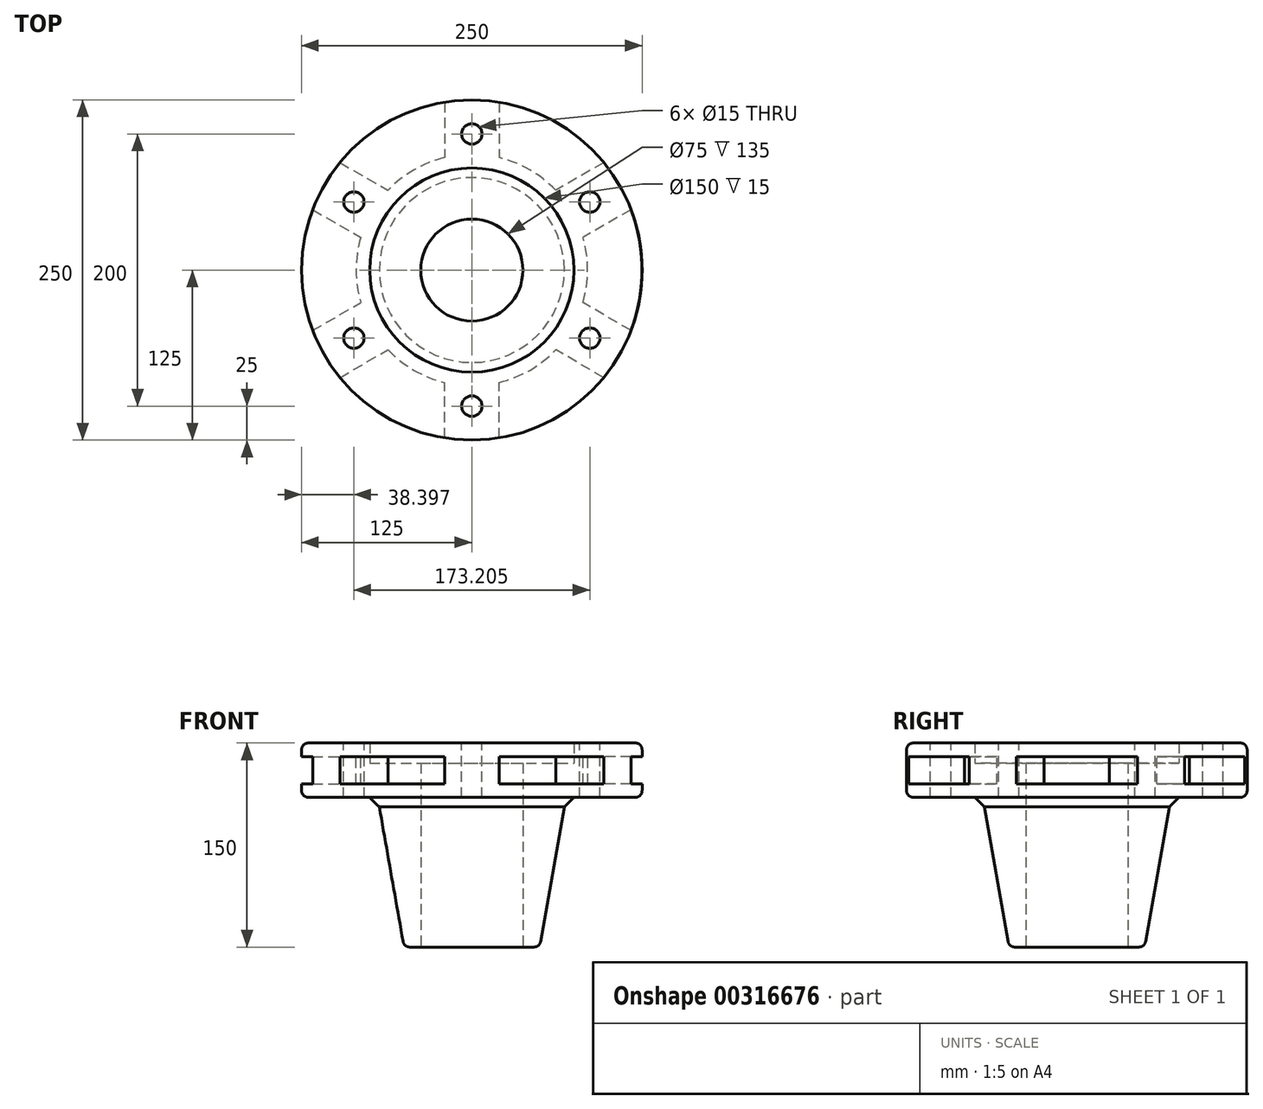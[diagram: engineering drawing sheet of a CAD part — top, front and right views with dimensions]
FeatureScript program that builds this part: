
annotation { "Feature Type Name" : "Feature", "Feature Type Description" : "" }
export const myFeature = defineFeature(function(context is Context, id is Id, definition is map)
    precondition{}
    {
        {
            var Q0;
            Q0=qCreatedBy(makeId("Front.planeOp"),FACE);
            var sketch = newSketch(context, id + "F0", { "sketchPlane" : qUnion([Q0])});
            skLineSegment(sketch, "E0", {"start": v(0, 0) * mm, "end": v(0, 150) * mm, "construction": true});
            skLineSegment(sketch, "E1", {"start": v(-37.5, 135) * mm, "end": v(-37.5, 0) * mm});
            skLineSegment(sketch, "E2", {"start": v(-37.5, 0) * mm, "end": v(-49.78, 0) * mm});
            skLineSegment(sketch, "E3", {"start": v(-49.78, 0) * mm, "end": v(-67.93, 102.93) * mm});
            skLineSegment(sketch, "E4", {"start": v(-75, 110) * mm, "end": v(-125, 110) * mm});
            skLineSegment(sketch, "E5", {"start": v(-125, 110) * mm, "end": v(-125, 150) * mm});
            skLineSegment(sketch, "E6", {"start": v(-125, 150) * mm, "end": v(-75, 150) * mm});
            skLineSegment(sketch, "E7", {"start": v(-75, 150) * mm, "end": v(-75, 135) * mm});
            skLineSegment(sketch, "E8", {"start": v(-75, 135) * mm, "end": v(-37.5, 135) * mm});
            skLineSegment(sketch, "E9", {"start": v(-67.93, 102.93) * mm, "end": v(-75, 110) * mm});
            skSolve(sketch);
        }
        {
            var Q0;
            Q0=makeQuery(id+"F0.imprint","IMPRINT",FACE,{"disambiguationData":[TD([[makeQuery(id+"F0.imprint","IMPRINT",EDGE,{"derivedFrom":sQuery(id+"F0.wireOp",EDGE,"E1")}),-1.0]])]});
            var Q1;
            Q1=sQuery(id+"F0.wireOp",EDGE,"E0");
            revolve(context, id + "F1", {"entities" : qUnion([Q0]), "axis" : qUnion([Q1]), "revolveType" : RevolveType.FULL});
        }
        {
            var Q0;
            Q0=makeQuery(id+"F1.opRevolve","SWEPT_FACE",FACE,{"disambiguationData":[OSD([sQuery(id+"F0.wireOp",EDGE,"E6")])]});
            cPlane(context, id + "F2", {"entities" : qUnion([Q0]), "cplaneType" : CPlaneType.OFFSET, "offset" : 10 * mm, "oppositeDirection" : true, "width" : 150 * mm, "height" : 150 * mm});
        }
        {
            var Q0;
            Q0=qCreatedBy(id+"F2.planeOp",FACE);
            var sketch = newSketch(context, id + "F3", { "sketchPlane" : qUnion([Q0])});
            skCircle(sketch, "E10", {"center": v(0, 0) * mm, "radius": 85 * mm});
            skCircle(sketch, "E11", {"center": v(0, 0) * mm, "radius": 100 * mm, "construction": true});
            skPoint(sketch, "E12", {"position": v(0, 100) * mm});
            skPoint(sketch, "E13.1.0", {"position": v(-86.6, 50) * mm});
            skPoint(sketch, "E13.2.0", {"position": v(-86.6, -50) * mm});
            skPoint(sketch, "E13.3.0", {"position": v(0, -100) * mm});
            skPoint(sketch, "E13.4.0", {"position": v(86.6, -50) * mm});
            skPoint(sketch, "E13.5.0", {"position": v(86.6, 50) * mm});
            skLineSegment(sketch, "E14", {"start": v(-20, 123.39) * mm, "end": v(-20, 82.61) * mm});
            skLineSegment(sketch, "E15", {"start": v(20, 123.39) * mm, "end": v(20, 82.61) * mm});
            skPoint(sketch, "E16.center", {"position": v(-16.81, 5.93) * mm});
            skCircle(sketch, "E17", {"center": v(0, 0) * mm, "radius": 125 * mm});
            skLineSegment(sketch, "E18.1.0", {"start": v(-116.86, 44.37) * mm, "end": v(-81.55, 23.99) * mm});
            skLineSegment(sketch, "E18.1.1", {"start": v(-96.86, 79.02) * mm, "end": v(-61.55, 58.63) * mm});
            skLineSegment(sketch, "E18.2.0", {"start": v(-96.86, -79.02) * mm, "end": v(-61.55, -58.63) * mm});
            skLineSegment(sketch, "E18.2.1", {"start": v(-116.86, -44.37) * mm, "end": v(-81.55, -23.99) * mm});
            skLineSegment(sketch, "E18.3.0", {"start": v(20, -123.39) * mm, "end": v(20, -82.61) * mm});
            skLineSegment(sketch, "E18.3.1", {"start": v(-20, -123.39) * mm, "end": v(-20, -82.61) * mm});
            skLineSegment(sketch, "E18.4.0", {"start": v(116.86, -44.37) * mm, "end": v(81.55, -23.99) * mm});
            skLineSegment(sketch, "E18.4.1", {"start": v(96.86, -79.02) * mm, "end": v(61.55, -58.63) * mm});
            skLineSegment(sketch, "E18.5.0", {"start": v(96.86, 79.02) * mm, "end": v(61.55, 58.63) * mm});
            skLineSegment(sketch, "E18.5.1", {"start": v(116.86, 44.37) * mm, "end": v(81.55, 23.99) * mm});
            skSolve(sketch);
        }
        {
            var Q0;
            {var subQ0=sQuery(id+"F3.wireOp",EDGE,"E14");Q0=makeQuery(id+"F3.imprint","IMPRINT",FACE,{"disambiguationData":[TD([[makeQuery(id+"F3.imprint","IMPRINT",EDGE,{"derivedFrom":subQ0}),-1.0]])]});}
            var Q1;
            {var subQ0=sQuery(id+"F3.wireOp",EDGE,"E15");Q1=makeQuery(id+"F3.imprint","IMPRINT",FACE,{"disambiguationData":[TD([[makeQuery(id+"F3.imprint","IMPRINT",EDGE,{"derivedFrom":subQ0}),1.0]])]});}
            var Q2;
            {var subQ0=sQuery(id+"F3.wireOp",EDGE,"E18.4.0");Q2=makeQuery(id+"F3.imprint","IMPRINT",FACE,{"disambiguationData":[TD([[makeQuery(id+"F3.imprint","IMPRINT",EDGE,{"derivedFrom":subQ0}),-1.0]])]});}
            var Q3;
            {var subQ0=sQuery(id+"F3.wireOp",EDGE,"E18.3.0");Q3=makeQuery(id+"F3.imprint","IMPRINT",FACE,{"disambiguationData":[TD([[makeQuery(id+"F3.imprint","IMPRINT",EDGE,{"derivedFrom":subQ0}),-1.0]])]});}
            var Q4;
            {var subQ0=sQuery(id+"F3.wireOp",EDGE,"E18.2.0");Q4=makeQuery(id+"F3.imprint","IMPRINT",FACE,{"disambiguationData":[TD([[makeQuery(id+"F3.imprint","IMPRINT",EDGE,{"derivedFrom":subQ0}),-1.0]])]});}
            var Q5;
            {var subQ0=sQuery(id+"F3.wireOp",EDGE,"E18.1.0");Q5=makeQuery(id+"F3.imprint","IMPRINT",FACE,{"disambiguationData":[TD([[makeQuery(id+"F3.imprint","IMPRINT",EDGE,{"derivedFrom":subQ0}),-1.0]])]});}
            extrude(context, id + "F4", {"entities" : qUnion([Q0, Q1, Q2, Q3, Q4, Q5]), "operationType" : NewBodyOperationType.REMOVE, "oppositeDirection" : true, "depth" : 20 * mm});
        }
        {
            var Q0;
            Q0=makeQuery(id+"F1.opRevolve","SWEPT_EDGE",EDGE,{"disambiguationData":[OSD([sQuery(id+"F0.wireOp",EDGE,"E5"),sQuery(id+"F0.wireOp",EDGE,"E6")])]});
            var Q1;
            Q1=makeQuery(id+"F1.opRevolve","SWEPT_EDGE",EDGE,{"disambiguationData":[OSD([sQuery(id+"F0.wireOp",EDGE,"E4"),sQuery(id+"F0.wireOp",EDGE,"E5")])]});
            var Q2;
            Q2=makeQuery(id+"F1.opRevolve","SWEPT_EDGE",EDGE,{"disambiguationData":[OSD([sQuery(id+"F0.wireOp",EDGE,"E2"),sQuery(id+"F0.wireOp",EDGE,"E3")])]});
            fillet(context, id + "F5", {"entities" : qUnion([Q0, Q1, Q2]), "radius" : 5 * mm, "tangentPropagation" : true, "allowEdgeOverflow" : false});
        }
        {
            var Q0;
            Q0=makeQuery(id+"F1.opRevolve","SWEPT_FACE",FACE,{"disambiguationData":[OSD([sQuery(id+"F0.wireOp",EDGE,"E6")])]});
            var sketch = newSketch(context, id + "F6", { "sketchPlane" : qUnion([Q0])});
            skPoint(sketch, "E19.0", {"position": v(0, 100) * mm});
            skPoint(sketch, "E20.0", {"position": v(86.6, 50) * mm});
            skPoint(sketch, "E21.0", {"position": v(86.6, -50) * mm});
            skPoint(sketch, "E22.0", {"position": v(0, -100) * mm});
            skPoint(sketch, "E23.0", {"position": v(-86.6, -50) * mm});
            skPoint(sketch, "E24.0", {"position": v(-86.6, 50) * mm});
            skSolve(sketch);
        }
        {
            var Q0;
            Q0=sQuery(id+"F6.wireOp",VERTEX,"E20.0");
            var Q1;
            Q1=sQuery(id+"F6.wireOp",VERTEX,"E21.0");
            var Q2;
            Q2=sQuery(id+"F6.wireOp",VERTEX,"E22.0");
            var Q3;
            Q3=sQuery(id+"F6.wireOp",VERTEX,"E23.0");
            var Q4;
            Q4=sQuery(id+"F6.wireOp",VERTEX,"E24.0");
            var Q5;
            Q5=sQuery(id+"F6.wireOp",VERTEX,"E19.0");
            var Q6;
            Q6=makeQuery(id+"F1.opRevolve","SWEPT_BODY",BODY,{"disambiguationData":[OSD([sQuery(id+"F0.wireOp",EDGE,"E1"),sQuery(id+"F0.wireOp",EDGE,"E2"),sQuery(id+"F0.wireOp",EDGE,"E3"),sQuery(id+"F0.wireOp",EDGE,"E4"),sQuery(id+"F0.wireOp",EDGE,"E5"),sQuery(id+"F0.wireOp",EDGE,"E6"),sQuery(id+"F0.wireOp",EDGE,"E7"),sQuery(id+"F0.wireOp",EDGE,"E8")])]});
            hole(context, id + "F7", {"style" : HoleStyle.SIMPLE, "endStyle" : HoleEndStyle.THROUGH, "holeDiameter" : 15 * mm, "tappedDepth" : 12 * mm, "tapClearance" : 3, "startFromSketch" : true, "locations" : qUnion([Q0, Q1, Q2, Q3, Q4, Q5]), "scope" : qUnion([Q6])});
        }
    });
